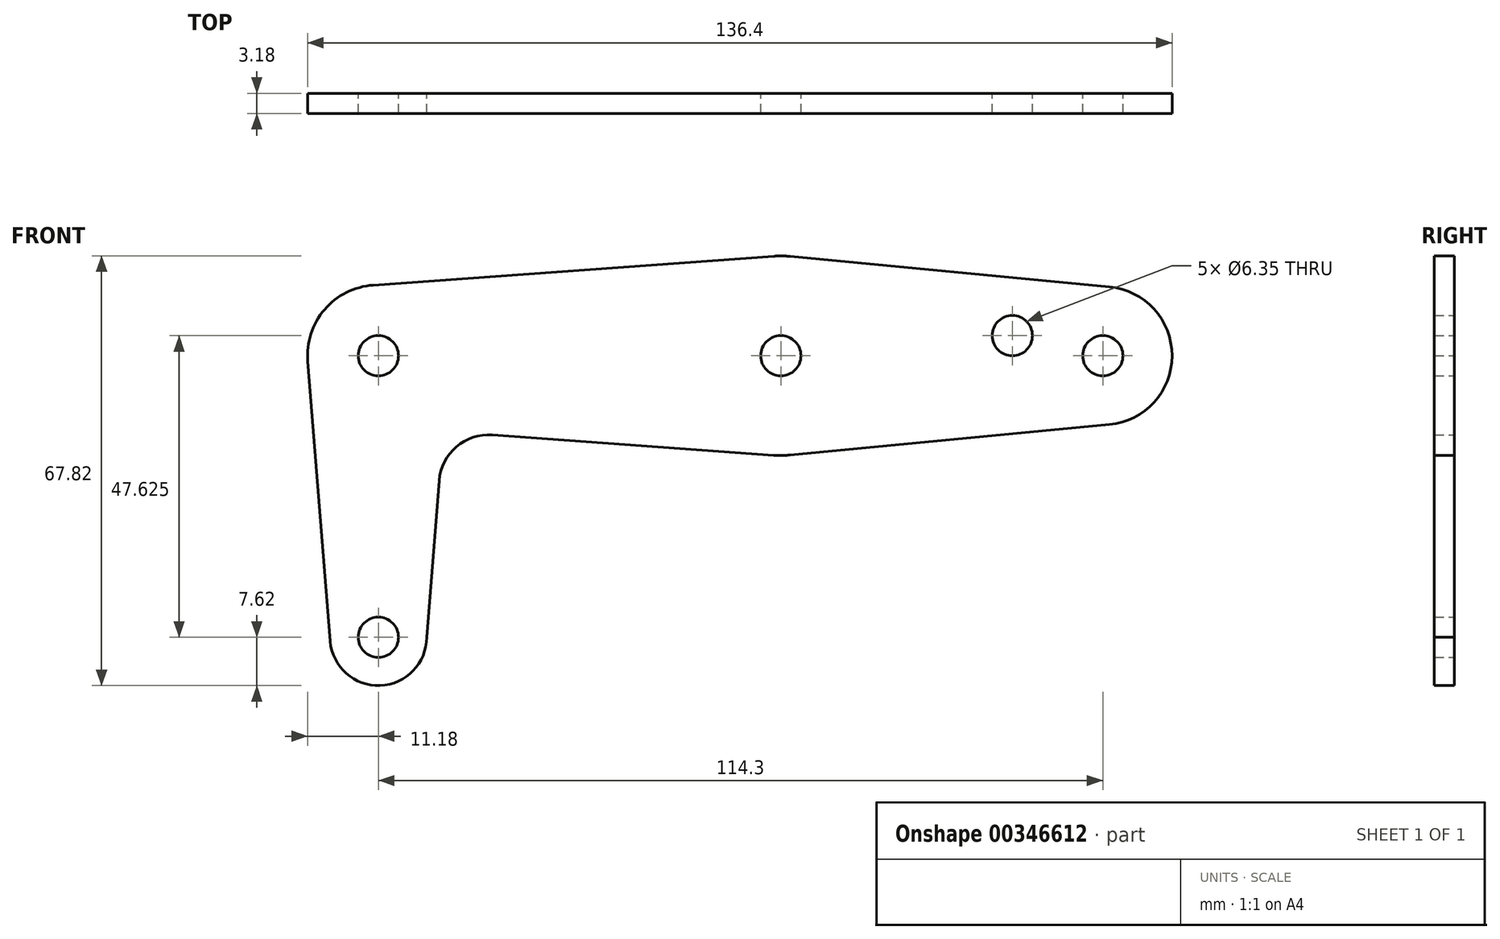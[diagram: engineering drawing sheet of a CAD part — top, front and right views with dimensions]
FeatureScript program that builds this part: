
annotation { "Feature Type Name" : "Feature", "Feature Type Description" : "" }
export const myFeature = defineFeature(function(context is Context, id is Id, definition is map)
    precondition{}
    {
        {
            var Q0;
            Q0=qCreatedBy(makeId("Front.planeOp"),FACE);
            var sketch = newSketch(context, id + "F0", { "sketchPlane" : qUnion([Q0])});
            skCircle(sketch, "E0", {"center": v(0, 0) * mm, "radius": 7.62 * mm});
            skCircle(sketch, "E1", {"center": v(0, 44.45) * mm, "radius": 11.18 * mm});
            skLineSegment(sketch, "E2", {"start": v(0, 44.45) * mm, "end": v(63.5, 44.45) * mm});
            skLineSegment(sketch, "E3", {"start": v(0, 44.45) * mm, "end": v(0, 0) * mm});
            skCircle(sketch, "E4", {"center": v(63.5, 44.45) * mm, "radius": 15.75 * mm});
            skLineSegment(sketch, "E5", {"start": v(63.5, 44.45) * mm, "end": v(114.3, 44.45) * mm});
            skCircle(sketch, "E6", {"center": v(114.3, 44.45) * mm, "radius": 10.92 * mm});
            skLineSegment(sketch, "E7", {"start": v(65, 60.13) * mm, "end": v(115.34, 55.32) * mm});
            skLineSegment(sketch, "E8", {"start": v(62.37, 60.16) * mm, "end": v(-0.8, 55.6) * mm});
            skLineSegment(sketch, "E9", {"start": v(115.34, 33.58) * mm, "end": v(65, 28.77) * mm});
            skLineSegment(sketch, "E10", {"start": v(7.62, 0) * mm, "end": v(9.58, 24.72) * mm});
            skLineSegment(sketch, "E11", {"start": v(62.37, 28.74) * mm, "end": v(18, 31.95) * mm});
            skPoint(sketch, "E12.visualSharp", {"position": v(10.2, 32.5) * mm});
            skArc(sketch, "E12.filletArc", {"start": v(18, 31.95) * mm, "mid": v(12.3, 30.06) * mm, "end": v(9.58, 24.72) * mm});
            skCircle(sketch, "E13", {"center": v(0, 0) * mm, "radius": 3.18 * mm});
            skCircle(sketch, "E14", {"center": v(0, 44.45) * mm, "radius": 3.18 * mm});
            skCircle(sketch, "E15", {"center": v(63.5, 44.45) * mm, "radius": 3.18 * mm});
            skCircle(sketch, "E16", {"center": v(114.3, 44.45) * mm, "radius": 3.18 * mm});
            skCircle(sketch, "E17", {"center": v(100.03, 47.62) * mm, "radius": 3.18 * mm});
            skLineSegment(sketch, "E18", {"start": v(-11.14, 43.56) * mm, "end": v(-7.6, -0.6) * mm});
            skSolve(sketch);
        }
        {
            var Q0;
            Q0=makeQuery(id+"F0.imprint","IMPRINT",FACE,{"disambiguationData":[TD([[makeQuery(id+"F0.imprint","IMPRINT",EDGE,{"derivedFrom":sQuery(id+"F0.wireOp",EDGE,"E13")}),-1.0]])]});
            var Q1;
            {var subQ0=sQuery(id+"F0.wireOp",EDGE,"E18");Q1=makeQuery(id+"F0.imprint","IMPRINT",FACE,{"disambiguationData":[TD([[makeQuery(id+"F0.imprint","IMPRINT",EDGE,{"derivedFrom":subQ0}),1.0]])]});}
            var Q2;
            {var subQ0=sQuery(id+"F0.wireOp",EDGE,"E8");Q2=makeQuery(id+"F0.imprint","IMPRINT",FACE,{"disambiguationData":[TD([[makeQuery(id+"F0.imprint","IMPRINT",EDGE,{"derivedFrom":subQ0}),1.0]])]});}
            var Q3;
            {var subQ0=sQuery(id+"F0.wireOp",EDGE,"E9");Q3=makeQuery(id+"F0.imprint","IMPRINT",FACE,{"disambiguationData":[TD([[makeQuery(id+"F0.imprint","IMPRINT",EDGE,{"derivedFrom":subQ0}),-1.0]])]});}
            var Q4;
            Q4=makeQuery(id+"F0.imprint","IMPRINT",FACE,{"disambiguationData":[TD([[makeQuery(id+"F0.imprint","IMPRINT",EDGE,{"derivedFrom":sQuery(id+"F0.wireOp",EDGE,"E16")}),-1.0]])]});
            var Q5;
            {var subQ0=sQuery(id+"F0.wireOp",EDGE,"E1");var subQ4=makeQuery(id+"F0.imprint","INTERSECT",VERTEX,{"derivedFrom":[subQ0,sQuery(id+"F0.wireOp",EDGE,"E8")]});Q5=makeQuery(id+"F0.imprint","IMPRINT",FACE,{"disambiguationData":[TD([[makeQuery(id+"F0.imprint","IMPRINT",EDGE,{"disambiguationData":[TD([[subQ4,1.0]])],"derivedFrom":subQ0}),1.0]])]});}
            var Q6;
            {var subQ0=sQuery(id+"F0.wireOp",EDGE,"E4");var subQ2=sQuery(id+"F0.wireOp",EDGE,"E2");var subQ3=makeQuery(id+"F0.imprint","INTERSECT",VERTEX,{"derivedFrom":[subQ2,subQ0]});Q6=makeQuery(id+"F0.imprint","IMPRINT",FACE,{"disambiguationData":[TD([[makeQuery(id+"F0.imprint","IMPRINT",EDGE,{"disambiguationData":[TD([[subQ3,-1.0]])],"derivedFrom":subQ2}),1.0]])]});}
            var Q7;
            {var subQ0=sQuery(id+"F0.wireOp",EDGE,"E4");var subQ3=sQuery(id+"F0.wireOp",EDGE,"E2");var subQ4=makeQuery(id+"F0.imprint","INTERSECT",VERTEX,{"derivedFrom":[subQ3,subQ0]});Q7=makeQuery(id+"F0.imprint","IMPRINT",FACE,{"disambiguationData":[TD([[makeQuery(id+"F0.imprint","IMPRINT",EDGE,{"disambiguationData":[TD([[subQ4,-1.0]])],"derivedFrom":subQ3}),-1.0]])]});}
            var Q8;
            {var subQ7=sQuery(id+"F0.wireOp",EDGE,"E7");Q8=makeQuery(id+"F0.imprint","IMPRINT",FACE,{"disambiguationData":[TD([[makeQuery(id+"F0.imprint","IMPRINT",EDGE,{"derivedFrom":subQ7}),-1.0]])]});}
            var Q9;
            {var subQ0=sQuery(id+"F0.wireOp",EDGE,"E2");var subQ1=sQuery(id+"F0.wireOp",EDGE,"E1");var subQ2=makeQuery(id+"F0.imprint","INTERSECT",VERTEX,{"derivedFrom":[subQ1,subQ0]});Q9=makeQuery(id+"F0.imprint","IMPRINT",FACE,{"disambiguationData":[TD([[makeQuery(id+"F0.imprint","IMPRINT",EDGE,{"disambiguationData":[TD([[subQ2,1.0]])],"derivedFrom":subQ1}),1.0]])]});}
            var Q10;
            {var subQ9=sQuery(id+"F0.wireOp",EDGE,"E10");Q10=makeQuery(id+"F0.imprint","IMPRINT",FACE,{"disambiguationData":[TD([[makeQuery(id+"F0.imprint","IMPRINT",EDGE,{"derivedFrom":subQ9}),1.0]])]});}
            extrude(context, id + "F1", {"entities" : qUnion([Q0, Q1, Q2, Q3, Q4, Q5, Q6, Q7, Q8, Q9, Q10]), "depth" : 3.17 * mm});
        }
    });
